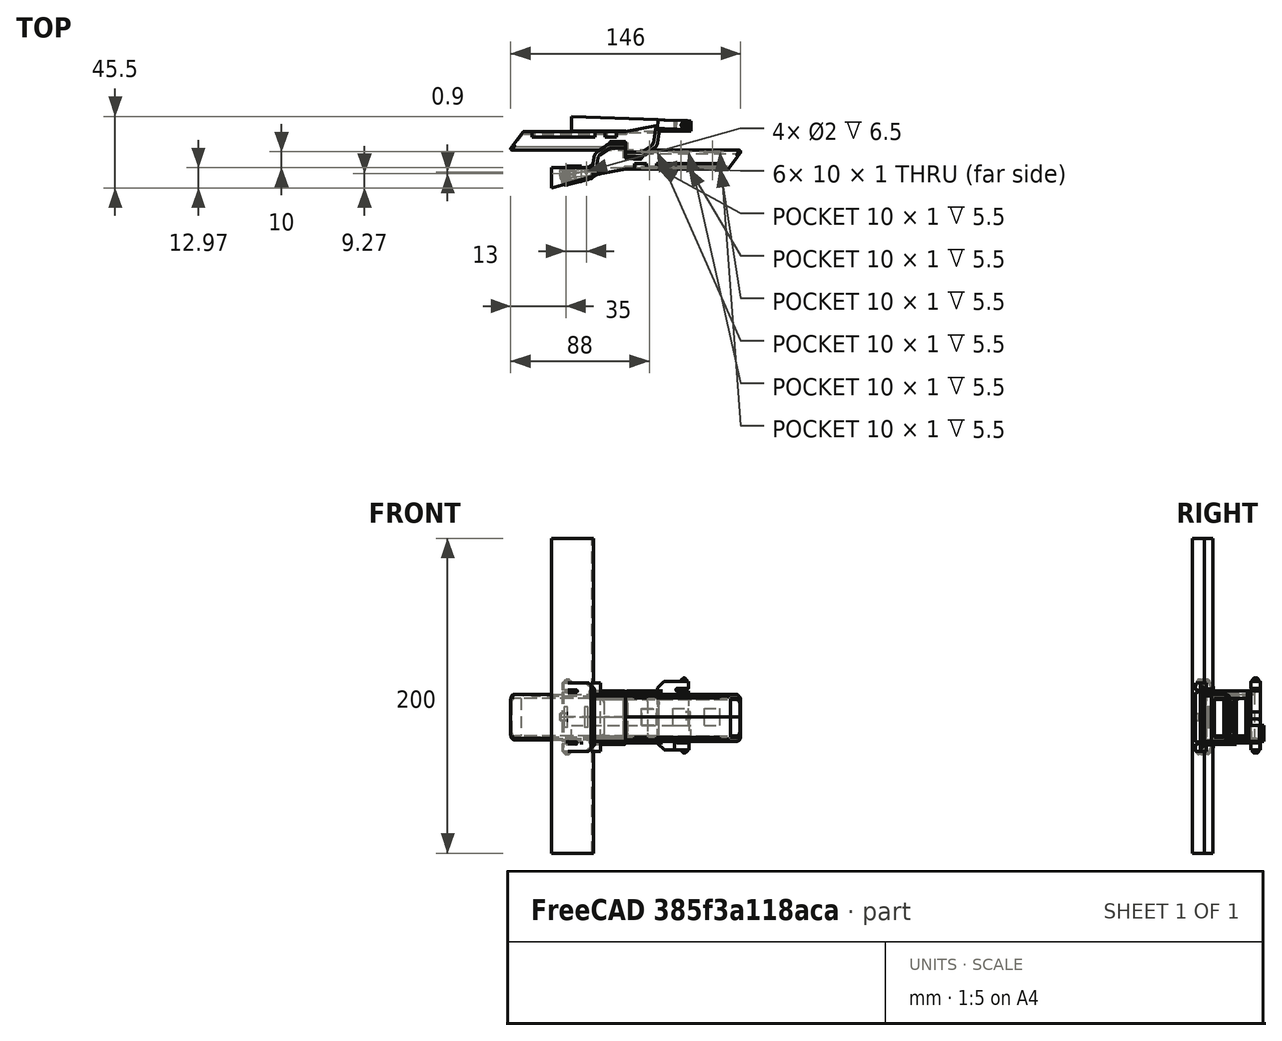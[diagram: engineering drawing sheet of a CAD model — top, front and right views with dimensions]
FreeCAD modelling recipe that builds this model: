
FCSTD DOCUMENT  (FreeCAD 0.20R29603 (Git))
Label: pieza_aspiradora_3
License: All rights reserved
LicenseURL: http://en.wikipedia.org/wiki/All_rights_reserved
objects: Part::Cut×28, Part::Box×22, Part::Feature×19, Sketcher::SketchObject×7, Mesh::Feature×7, PartDesign::Pad×6, PartDesign::Body×6, Part::Cylinder×4, Part::MultiFuse×3, Part::Chamfer×3, Part::Fillet×2, PartDesign::ShapeBinder×1, App::DocumentObjectGroup×1
note: 107 computed .brp shape members not serialized (recipe doc carries the construction recipe); baked Part::Feature solids carry a one-line shape summary decoded from their .brp

FEATURE [Part::Feature] Fillet003004004013003009007002  label="pieza_entera_version_023"
  shape: bbox 114.9 x 25.35 x 47.71 mm, 239 faces (baked)
FEATURE [Sketcher::SketchObject] Sketch
  FullyConstrained = false
  MapMode = 5
  Placement = pos=(0,0,29) rot=(0,0,1;0rad)
  sketch-geometry (4):
    g0: LineSegment StartX=-21.2444 StartY=-11.0491 StartZ=0 EndX=-47.216 EndY=-11.0491 EndZ=0
    g1: LineSegment StartX=-47.216 StartY=-11.0491 StartZ=0 EndX=-47.216 EndY=-23.9668 EndZ=0
    g2: LineSegment StartX=-47.216 StartY=-23.9668 StartZ=0 EndX=-20.2912 EndY=-16.4659 EndZ=0
    g3: LineSegment StartX=-20.2912 StartY=-16.4659 StartZ=0 EndX=-21.2444 EndY=-11.0491 EndZ=0
  constraints (6):
    c: Horizontal(g0)
    c: Coincident(g0,g1)
    c: Vertical(g1)
    c: Coincident(g1,g2)
    c: Coincident(g2,g3)
    c: Coincident(g3,g0)
FEATURE [Part::Feature] Fillet003004004013003009007001  label="pieza_entera_version_022"
  shape: bbox 114.9 x 25.35 x 47.71 mm, 239 faces (baked)
FEATURE [PartDesign::Pad] Pad
  Direction = (0,0,1)
  Length = 200
  Length2 = 10
  Midplane = true
  Placement = pos=(0,0,29) rot=(0,0,1;0rad)
  Profile = -> Sketch
  ReferenceAxis = -> Sketch [N_Axis]
  Type = 0
FEATURE [PartDesign::Body] Body
  Group = -> [Sketch,Pad]
  Origin = -> Origin
  Tip = -> Pad
FEATURE [Part::Feature] Fillet003004004013003009007001001  label="pieza_entera_version_024"
  shape: bbox 114.9 x 25.35 x 47.71 mm, 239 faces (baked)
FEATURE [Part::Cut] Cut  label="atras"
  Base = -> Fillet003004004013003009007001
  Tool = -> Body
FEATURE [Part::Feature] Body001
  shape: bbox 26.92 x 12.92 x 200 mm, 6 faces (baked)
FEATURE [Sketcher::SketchObject] Sketch001
  ExternalGeometry = -> [Body001]
  FullyConstrained = false
  MapMode = 2
  Support = -> [Body001]
  sketch-geometry (8):
    g0: LineSegment StartX=-21.2444 StartY=-11.0491 StartZ=0 EndX=-20.2912 EndY=-16.4659 EndZ=0
    g1: LineSegment StartX=-20.2912 StartY=-16.4659 StartZ=0 EndX=-20.2912 EndY=-35.922 EndZ=0
    g2: LineSegment StartX=-20.2912 StartY=-35.922 StartZ=0 EndX=80.7898 EndY=-35.922 EndZ=0
    g3: LineSegment StartX=80.7898 StartY=-35.922 StartZ=0 EndX=80.7898 EndY=22.648 EndZ=0
    g4: LineSegment StartX=80.7898 StartY=22.648 StartZ=0 EndX=-28.5502 EndY=22.648 EndZ=0
    g5: LineSegment StartX=-28.5502 StartY=22.648 StartZ=0 EndX=-21.2444 EndY=-11.0491 EndZ=0
    g6: LineSegment StartX=-21.2444 StartY=-11.0491 StartZ=0 EndX=-20.2912 EndY=-16.4659 EndZ=0
    g7: LineSegment StartX=-21.2444 StartY=-11.0491 StartZ=0 EndX=-20.2912 EndY=-16.4659 EndZ=0
  constraints (17):
    c: Coincident(g-3,g0)
    c: Coincident(g0,g1)
    c: Vertical(g1)
    c: Coincident(g1,g2)
    c: Horizontal(g2)
    c: Coincident(g2,g3)
    c: Vertical(g3)
    c: Coincident(g3,g4)
    c: Horizontal(g4)
    c: Coincident(g4,g5)
    c: Coincident(g5,g0)
    c: Coincident(g6,g0)
    c: Coincident(g6,g0)
    c: DistanceX(g4,g4) = 109.34
    c: Coincident(g0,g-3)
    c: Coincident(g7,g0)
    c: Coincident(g7,g0)
FEATURE [PartDesign::ShapeBinder] ShapeBinder
  Support = -> [Sketch001]
  TraceSupport = false
FEATURE [PartDesign::Pad] Pad001
  Direction = (0,0,1)
  Length = 200
  Length2 = 10
  Midplane = true
  Profile = -> ShapeBinder
  Type = 0
FEATURE [PartDesign::Body] Body002
  Group = -> [ShapeBinder,Pad001]
  Origin = -> Origin001
  Tip = -> Pad001
FEATURE [Part::Cut] Cut001  label="adelante"
  Base = -> Fillet003004004013003009007001001
  Tool = -> Body002
FEATURE [Part::Feature] Cut002  label="atras001"
  shape: bbox 94.45 x 22.12 x 35.49 mm, 153 faces (baked)
FEATURE [Part::Feature] Cut003  label="atras002"
  shape: bbox 94.45 x 22.12 x 35.49 mm, 153 faces (baked)
FEATURE [Part::Feature] Cut001001  label="atras_final__4.8_grados"
  Placement = pos=(1.4,-1.58,0) rot=(0,0,-1;0.095993rad)
  shape: bbox 21.29 x 6.944 x 47.71 mm, 93 faces (baked)
FEATURE [Part::Feature] Cut001002  label="adelante002"
  shape: bbox 21.48 x 8.668 x 47.71 mm, 93 faces (baked)
FEATURE [Part::Box] Box  label="Cube"
  AttacherType = Attacher::AttachEngine3D
  Height = 10
  Length = 11
  Placement = pos=(-28,-31,-12) rot=(0,0,1;0rad)
  Width = 60
FEATURE [Part::Box] Box001  label="Cube001"
  AttacherType = Attacher::AttachEngine3D
  Height = 10
  Length = 11
  Placement = pos=(-28,-31,31) rot=(0,0,1;0rad)
  Width = 60
FEATURE [Part::Cut] Cut001003
  Base = -> Cut002
  Tool = -> Box
FEATURE [Part::Cut] Cut001004  label="adekante11"
  Base = -> Cut001003
  Tool = -> Box001
FEATURE [Part::Box] Box002  label="Cube002"
  AttacherType = Attacher::AttachEngine3D
  Height = 200
  Length = 23.97
  Placement = pos=(-20,-35.96,-14) rot=(0,0,1;0.179769rad)
  Width = 20
FEATURE [Part::Cut] Cut001005  label="adelante_final"
  Base = -> Cut001004
  Placement = pos=(0,0,0.91) rot=(0,0,1;0rad)
  Tool = -> Box002
FEATURE [Mesh::Feature] Mesh  label="atras1 (Meshed)"
FEATURE [Mesh::Feature] Mesh001  label="adelante1 (Meshed)"
FEATURE [Sketcher::SketchObject] Sketch002
  ExternalGeometry = -> [Cut001005,Cut001001]
  FullyConstrained = true
  MapMode = 5
  Placement = pos=(0,0,29.91) rot=(0,0,1;0rad)
  Support = -> [Cut001005]
  constraints (2):
    c: Angle(g-4) = 0
    c: Angle(g-3,g-5) = 2.96182
FEATURE [Part::Feature] Cut001001001  label="atras1_4.8_grados001"
  Placement = pos=(1.4,-1.58,0) rot=(0,0,-1;0.095993rad)
  shape: bbox 21.29 x 6.944 x 47.71 mm, 93 faces (baked)
FEATURE [Part::Feature] Cut001005001  label="adelante003"
  Placement = pos=(0,0,0.91) rot=(0,0,1;0rad)
  shape: bbox 94.45 x 21.36 x 33 mm, 154 faces (baked)
FEATURE [Part::MultiFuse] Fusion
  Shapes = -> [Cut001001001,Cut001005001]
FEATURE [Part::Chamfer] Chamfer
  Base = -> Fusion
  Edges = 2 edges r=2: [Edge27,Edge28]
FEATURE [Part::Chamfer] Chamfer001
  Base = -> Chamfer
  Edges = 2 edges r=2: [Edge8,Edge9]
FEATURE [Part::Chamfer] Chamfer002  label="modelo_grados_48"
  Base = -> Chamfer001
  Edges = 1 edges r=0.29: [Edge244]
FEATURE [Part::Feature] Chamfer002001  label="modelo_grados_48_1"
  shape: bbox 114.8 x 23.12 x 47.71 mm, 250 faces (baked)
FEATURE [Part::Feature] Chamfer002002  label="modelo_grados_48_2"
  shape: bbox 114.8 x 23.12 x 47.71 mm, 250 faces (baked)
FEATURE [Part::Box] Box003  label="Cube003"
  AttacherType = Attacher::AttachEngine3D
  Height = 50
  Length = 150
  Placement = pos=(-70,-28,15.5) rot=(0,0,1;0rad)
  Width = 50
FEATURE [Part::Box] Box004  label="Cube004"
  AttacherType = Attacher::AttachEngine3D
  Height = 50
  Length = 150
  Placement = pos=(-70,-28,-34.5) rot=(0,0,1;0rad)
  Width = 50
FEATURE [Part::Cut] Cut001005002
  Base = -> Chamfer002001
  Tool = -> Box003
FEATURE [Part::Cut] Cut001005003
  Base = -> Chamfer002002
  Tool = -> Box004
FEATURE [Part::Box] Box055  label="Cube054"
  AttacherType = Attacher::AttachEngine3D
  Height = 9
  Length = 10
  Placement = pos=(30,-1.5,12) rot=(0,0,1;0rad)
  Width = 1
FEATURE [Part::Box] Box062  label="cunia1"
  AttacherType = Attacher::AttachEngine3D
  Height = 1.6
  Length = 10
  Placement = pos=(-38,-20,-1.8) rot=(0,0,1;0rad)
  Width = 10
FEATURE [Part::Box] Box050  label="Cube049"
  AttacherType = Attacher::AttachEngine3D
  Height = 9
  Length = 10
  Placement = pos=(50,-1.5,12) rot=(0,0,1;0rad)
  Width = 1
FEATURE [Part::Box] Box051  label="Cube050"
  AttacherType = Attacher::AttachEngine3D
  Height = 9
  Length = 10
  Placement = pos=(50,-11.5,12) rot=(0,0,1;0rad)
  Width = 1
FEATURE [Part::Box] Box052  label="Cube051"
  AttacherType = Attacher::AttachEngine3D
  Height = 9
  Length = 10
  Placement = pos=(30,-11.5,12) rot=(0,0,1;0rad)
  Width = 1
FEATURE [Part::Box] Box053  label="Cube052"
  AttacherType = Attacher::AttachEngine3D
  Height = 9
  Length = 10
  Placement = pos=(10,-11.5,12) rot=(0,0,1;0rad)
  Width = 1
FEATURE [Part::Box] Box054  label="Cube053"
  AttacherType = Attacher::AttachEngine3D
  Height = 9
  Length = 10
  Placement = pos=(10,-1.5,12) rot=(0,0,1;0rad)
  Width = 1
FEATURE [Part::Cylinder] Cylinder012
  Angle = 360
  AttacherType = Attacher::AttachEngine3D
  FirstAngle = 0
  Height = 10
  Placement = pos=(-25,-13.8,9) rot=(0,0,1;0rad)
  Radius = 1
  SecondAngle = 0
FEATURE [Part::Cylinder] Cylinder013
  Angle = 360
  AttacherType = Attacher::AttachEngine3D
  FirstAngle = 0
  Height = 10
  Placement = pos=(-38,-14.7,9) rot=(0,0,1;0rad)
  Radius = 1
  SecondAngle = 0
FEATURE [Part::Box] Box063  label="Cube055"
  AttacherType = Attacher::AttachEngine3D
  Height = 9
  Length = 10
  Placement = pos=(50,-1.5,10) rot=(0,0,1;0rad)
  Width = 1
FEATURE [Part::Box] Box064  label="Cube056"
  AttacherType = Attacher::AttachEngine3D
  Height = 9
  Length = 10
  Placement = pos=(50,-11.5,10) rot=(0,0,1;0rad)
  Width = 1
FEATURE [Part::Box] Box065  label="Cube057"
  AttacherType = Attacher::AttachEngine3D
  Height = 9
  Length = 10
  Placement = pos=(30,-11.5,10) rot=(0,0,1;0rad)
  Width = 1
FEATURE [Part::Box] Box066  label="Cube058"
  AttacherType = Attacher::AttachEngine3D
  Height = 9
  Length = 10
  Placement = pos=(10,-11.5,10) rot=(0,0,1;0rad)
  Width = 1
FEATURE [Part::Box] Box067  label="Cube059"
  AttacherType = Attacher::AttachEngine3D
  Height = 9
  Length = 10
  Placement = pos=(10,-1.5,10) rot=(0,0,1;0rad)
  Width = 1
FEATURE [Part::Box] Box068  label="Cube060"
  AttacherType = Attacher::AttachEngine3D
  Height = 9
  Length = 10
  Placement = pos=(30,-1.5,10) rot=(0,0,1;0rad)
  Width = 1
FEATURE [Part::Box] Box069  label="cunia"
  AttacherType = Attacher::AttachEngine3D
  Height = 1.4
  Length = 5
  Placement = pos=(-38.3,-17,31.22) rot=(0,0,1;0rad)
  Width = 5
FEATURE [Part::Cylinder] Cylinder014
  Angle = 360
  AttacherType = Attacher::AttachEngine3D
  FirstAngle = 0
  Height = 10
  Placement = pos=(-25,-13.8,12) rot=(0,0,1;0rad)
  Radius = 1
  SecondAngle = 0
FEATURE [Part::Cylinder] Cylinder015
  Angle = 360
  AttacherType = Attacher::AttachEngine3D
  FirstAngle = 0
  Height = 10
  Placement = pos=(-38,-14.7,12) rot=(0,0,1;0rad)
  Radius = 1
  SecondAngle = 0
FEATURE [Part::Cut] Cut001005004
  Base = -> Cut001005002
  Tool = -> Cylinder012
FEATURE [Part::Cut] Cut001005005
  Base = -> Cut001005004
  Tool = -> Cylinder013
FEATURE [Part::Cut] Cut001005006
  Base = -> Cut001005005
  Tool = -> Box063
FEATURE [Part::Cut] Cut001005007
  Base = -> Cut001005006
  Tool = -> Box064
FEATURE [Part::Cut] Cut001005008
  Base = -> Cut001005007
  Tool = -> Box065
FEATURE [Part::Cut] Cut001005009
  Base = -> Cut001005008
  Tool = -> Box066
FEATURE [Part::Cut] Cut001005010
  Base = -> Cut001005009
  Tool = -> Box067
FEATURE [Part::Cut] Cut001005011  label="parte_1_grados_4_8"
  Base = -> Cut001005010
  Tool = -> Box068
FEATURE [Part::Cut] Cut001005012
  Base = -> Cut001005003
  Tool = -> Cylinder014
FEATURE [Part::Cut] Cut001005013
  Base = -> Cut001005012
  Tool = -> Cylinder015
FEATURE [Part::Cut] Cut001005014
  Base = -> Cut001005013
  Tool = -> Box054
FEATURE [Part::Cut] Cut001005015
  Base = -> Cut001005014
  Tool = -> Box052
FEATURE [Part::Cut] Cut001005016
  Base = -> Cut001005015
  Tool = -> Box051
FEATURE [Part::Cut] Cut001005017
  Base = -> Cut001005016
  Tool = -> Box053
FEATURE [Part::Cut] Cut001005018
  Base = -> Cut001005017
  Tool = -> Box050
FEATURE [Part::Cut] Cut001005019  label="parte_2_grados_4_8"
  Base = -> Cut001005018
  Tool = -> Box055
FEATURE [Part::Box] Box041  label="uniones_planas"
  AttacherType = Attacher::AttachEngine3D
  Height = 10
  Length = 9
  Placement = pos=(10.5,-1.4,10.5) rot=(0,0,1;0rad)
  Width = 0.8
FEATURE [Mesh::Feature] Mesh002  label="cunia (Meshed)"
FEATURE [Mesh::Feature] Mesh003  label="parte_1_grados_4_8 (Meshed)"
FEATURE [Mesh::Feature] Mesh004  label="parte_2_grados_4_8 (Meshed)"
FEATURE [Mesh::Feature] Mesh005  label="uniones_planas (Meshed)"
FEATURE [App::DocumentObjectGroup] Group  label="finales_grados_4_8"
  Group = -> [Box069,Cut001005011,Cut001005019,Box041,Mesh002,Mesh003,Mesh004,Mesh005]
FEATURE [Part::Feature] Cut001005020  label="atras1_4.8_grados002"
  Placement = pos=(1.4,-1.58,0) rot=(0,0,-1;0.095993rad)
  shape: bbox 21.29 x 6.944 x 47.71 mm, 93 faces (baked)
FEATURE [Part::Feature] Cut001005021  label="adelante004"
  Placement = pos=(0,0,0.91) rot=(0,0,1;0rad)
  shape: bbox 94.45 x 21.36 x 33 mm, 154 faces (baked)
FEATURE [Part::Feature] Cut001005022  label="atras1_m4.8_grados003"
  Placement = pos=(-0.6,0.8,0) rot=(0,0,1;0.083776rad)
  shape: bbox 21.49 x 10.13 x 47.71 mm, 93 faces (baked)
FEATURE [Sketcher::SketchObject] Sketch003
  FullyConstrained = true
  MapMode = 5
  Support = -> [XY_Plane002]
  sketch-geometry (3):
    g0: LineSegment StartX=-18.12 StartY=-33.34 StartZ=0 EndX=-12.12 EndY=-33.34 EndZ=0
    g1: LineSegment StartX=-12.12 StartY=-33.34 StartZ=0 EndX=-12.12 EndY=-29.49 EndZ=0
    g2: ArcOfCircle CenterX=-11.0004 CenterY=-37.8352 CenterZ=0 NormalX=0 NormalY=0 NormalZ=1 AngleXU=0 Radius=8.42 StartAngle=1.70417 EndAngle=2.57842
  constraints (10):
    c: Horizontal(g0)
    c: Coincident(g0,g1)
    c: Vertical(g1)
    c: DistanceY(g1,g1) = 3.85
    c: DistanceX(g0,g0) = 6
    c: Coincident(g2,g0)
    c: Coincident(g1,g2)
    c: DistanceX(g0,g-1) = 18.12
    c: DistanceY(g0,g-1) = 33.34
    c: Radius(g2) = 8.42
FEATURE [PartDesign::Pad] Pad002
  Direction = (0,0,1)
  Length = 200
  Length2 = 10
  Midplane = true
  Profile = -> Sketch003
  ReferenceAxis = -> Sketch003 [N_Axis]
  Type = 0
FEATURE [PartDesign::Body] Body003
  Group = -> [Sketch003,Pad002]
  Origin = -> Origin002
  Placement = pos=(-4,14.56,0) rot=(0,0,1;0rad)
  Tip = -> Pad002
FEATURE [Part::Cut] Cut001005023  label="atras_cortado1"
  Base = -> Cut001005022
  Tool = -> Body003
FEATURE [Sketcher::SketchObject] Sketch004
  FullyConstrained = true
  MapMode = 5
  Support = -> [XY_Plane003]
  sketch-geometry (4):
    g0: LineSegment StartX=-18.12 StartY=-33.34 StartZ=0 EndX=-18.12 EndY=-29.49 EndZ=0
    g1: LineSegment StartX=-18.12 StartY=-29.49 StartZ=0 EndX=-12.12 EndY=-29.49 EndZ=0
    g2: GeomPoint X=-11 Y=-37.8358 Z=0
    g3: ArcOfCircle CenterX=-11 CenterY=-37.8358 CenterZ=0 NormalX=0 NormalY=0 NormalZ=1 AngleXU=0 Radius=8.4206 StartAngle=1.7042 EndAngle=2.57838
  constraints (11):
    c: Vertical(g0)
    c: Coincident(g0,g1)
    c: Horizontal(g1)
    c: DistanceX(g1,g1) = 6
    c: DistanceY(g0,g0) = 3.85
    c: DistanceX(g0,g-1) = 18.12
    c: DistanceY(g0,g-1) = 33.34
    c: DistanceX(g2,g-1) = 11
    c: Coincident(g3,g2)
    c: Coincident(g3,g0)
    c: Coincident(g1,g3)
FEATURE [PartDesign::Pad] Pad003
  Direction = (0,0,1)
  Length = 43.5
  Length2 = 10
  Midplane = true
  Profile = -> Sketch004
  ReferenceAxis = -> Sketch004 [N_Axis]
  Type = 0
FEATURE [PartDesign::Body] Body004
  Group = -> [Sketch004,Pad003]
  Origin = -> Origin003
  Placement = pos=(-4.03,14.58,15.5) rot=(0,0,1;0rad)
  Tip = -> Pad003
FEATURE [Part::Feature] Cut001005024  label="atras1_m4.8_grados004"
  Placement = pos=(-0.6,0.8,0) rot=(0,0,1;0.083776rad)
  shape: bbox 21.49 x 10.13 x 47.71 mm, 93 faces (baked)
FEATURE [Sketcher::SketchObject] Sketch005
  FullyConstrained = true
  MapMode = 5
  Support = -> [XY_Plane004]
  sketch-geometry (3):
    g0: LineSegment StartX=-18.12 StartY=-33.34 StartZ=0 EndX=-12.12 EndY=-33.34 EndZ=0
    g1: LineSegment StartX=-12.12 StartY=-33.34 StartZ=0 EndX=-12.12 EndY=-29.49 EndZ=0
    g2: ArcOfCircle CenterX=-11.0004 CenterY=-37.8352 CenterZ=0 NormalX=0 NormalY=0 NormalZ=1 AngleXU=0 Radius=8.42 StartAngle=1.70417 EndAngle=2.57842
  constraints (10):
    c: Horizontal(g0)
    c: Coincident(g0,g1)
    c: Vertical(g1)
    c: DistanceY(g1,g1) = 3.85
    c: DistanceX(g0,g0) = 6
    c: Coincident(g2,g0)
    c: Coincident(g1,g2)
    c: DistanceX(g0,g-1) = 18.12
    c: DistanceY(g0,g-1) = 33.34
    c: Radius(g2) = 8.42
FEATURE [PartDesign::Pad] Pad004
  Direction = (0,0,1)
  Length = 200
  Length2 = 10
  Midplane = true
  Profile = -> Sketch005
  ReferenceAxis = -> Sketch005 [N_Axis]
  Type = 0
FEATURE [PartDesign::Body] Body005
  Group = -> [Sketch005,Pad004]
  Origin = -> Origin004
  Placement = pos=(-4,14.56,0) rot=(0,0,1;0rad)
  Tip = -> Pad004
FEATURE [Part::Cut] Cut001005025  label="atras_cortado002"
  Base = -> Cut001005024
  Tool = -> Body005
FEATURE [Part::Cut] Cut001005026
  Base = -> Body004
  Tool = -> Cut001005025
FEATURE [Part::MultiFuse] Fusion001
  Shapes = -> [Cut001005021,Cut001005023]
FEATURE [Part::Fillet] Fillet  label="potencial4"
  Base = -> Fusion001
  Edges = 1 edges r=0.5: [Edge66]
FEATURE [Part::Feature] Cut001005027  label="atras1_4.8_grados003"
  Placement = pos=(-2.9,7.5,0.91) rot=(0,0,1;2.93215rad)
  shape: bbox 21.09 x 6.212 x 47.71 mm, 93 faces (baked)
FEATURE [Part::Feature] Cut001005028  label="adelante005"
  Placement = pos=(0,0,0.91) rot=(0,0,1;3.14159rad)
  shape: bbox 94.45 x 21.36 x 33 mm, 154 faces (baked)
FEATURE [Sketcher::SketchObject] Sketch006
  FullyConstrained = false
  MapMode = 5
  Support = -> [XY_Plane005]
  sketch-geometry (4):
    g0: LineSegment StartX=-82.4547 StartY=-24.1695 StartZ=0 EndX=-82.4547 EndY=-33.6695 EndZ=0
    g1: LineSegment StartX=-82.4547 StartY=-33.6695 StartZ=0 EndX=-6.45472 EndY=-33.6695 EndZ=0
    g2: LineSegment StartX=-6.45472 StartY=-33.6695 StartZ=0 EndX=-6.45472 EndY=-27.1695 EndZ=0
    g3: LineSegment StartX=-6.45472 StartY=-27.1695 StartZ=0 EndX=-82.4547 EndY=-24.1695 EndZ=0
  constraints (10):
    c: Coincident(g0,g1)
    c: Horizontal(g1)
    c: Coincident(g1,g2)
    c: Coincident(g2,g3)
    c: Coincident(g3,g0)
    c: Vertical(g0)
    c: Vertical(g2)
    c: DistanceY(g2,g2) = 6.5
    c: DistanceY(g0,g0) = 9.5
    c: DistanceX(g1,g1) = 76
FEATURE [PartDesign::Pad] Pad005
  Direction = (0,0,1)
  Length = 10
  Length2 = 10
  Profile = -> Sketch006
  ReferenceAxis = -> Sketch006 [N_Axis]
  Type = 0
FEATURE [PartDesign::Body] Body006
  Group = -> [Sketch006,Pad005]
  Origin = -> Origin005
  Placement = pos=(48,45.7,0) rot=(0,0,1;0rad)
  Tip = -> Pad005
FEATURE [Part::MultiFuse] Fusion002
  Shapes = -> [Cut001005027,Cut001005028]
FEATURE [Part::Fillet] Fillet003004004013003009007001002
  Base = -> Fusion002
  Edges = 1 edges r=2: [Edge23]
FEATURE [Part::Feature] Fillet003004004013003009007001002001  label="for_test_4"
  shape: bbox 114.4 x 25.04 x 47.71 mm, 248 faces (baked)
FEATURE [Part::Box] Box070  label="Cube061"
  AttacherType = Attacher::AttachEngine3D
  Height = 50
  Length = 136
  Placement = pos=(-84,-9,2) rot=(0,0,1;0rad)
  Width = 50
FEATURE [Part::Box] Box071  label="Cube062"
  AttacherType = Attacher::AttachEngine3D
  Height = 50
  Length = 120
  Placement = pos=(-89,-9,-49) rot=(0,0,1;0rad)
  Width = 50
FEATURE [Part::Cut] Cut001005029
  Base = -> Fillet003004004013003009007001002001
  Tool = -> Box070
FEATURE [Part::Cut] Cut001005030
  Base = -> Cut001005029
  Tool = -> Box071
FEATURE [Mesh::Feature] Mesh006  label="Cut001005030 (Meshed)"
